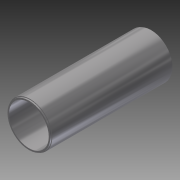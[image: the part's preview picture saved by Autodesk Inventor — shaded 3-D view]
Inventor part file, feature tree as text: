
AUTODESK INVENTOR PART (.ipt)
format: ipt  version: 2014 SP1 (Build 180222100, 222)  size: 93,184 bytes
history: native  units: in
note: dims shown in document units (in); Inventor stores cm internally (conversion verified against a paired STEP export)
features: sketch x2, extrude x1, revolve x1, mirror x1
ambient origin geometry x8: Origin, YZ Plane, XZ Plane, XY Plane, X Axis, Y Axis, Z Axis, Center Point
bodies: Solid1 (feature_tree)
feature tree (5):
  extrude  "Extrusion1"  Depth=0.1in
  revolve  "Revolution1"  [1 undecoded]
  mirror  "Mirror1"
  sketch  "Sketch1"  dims[d0=2.062in d1=0.1in]
  sketch  "Sketch2"  dims[d2=5.72in d3=0.0in d4=0.0625in d5=0.031in d6=90.0deg]
note: 1 required parameter value undecoded (feature->parameter linkage not recoverable at this tier; creation-order binding heuristic only, values carry confidence <= 0.55)
